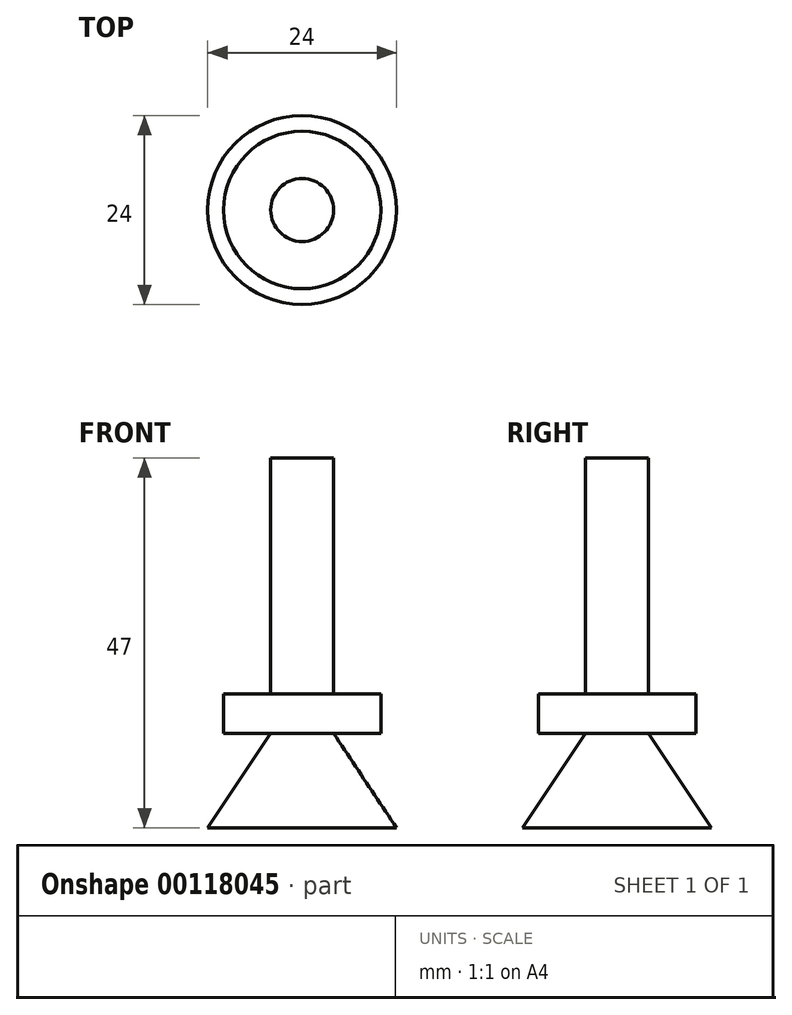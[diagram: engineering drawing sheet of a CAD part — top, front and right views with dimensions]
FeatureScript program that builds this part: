
annotation { "Feature Type Name" : "Feature", "Feature Type Description" : "" }
export const myFeature = defineFeature(function(context is Context, id is Id, definition is map)
    precondition{}
    {
        {
            var Q0;
            Q0=qCreatedBy(makeId("Front.planeOp"),FACE);
            var sketch = newSketch(context, id + "F0", { "sketchPlane" : qUnion([Q0])});
            skLineSegment(sketch, "E0.bottom", {"start": v(0, 0) * mm, "end": v(4, 0) * mm});
            skLineSegment(sketch, "E0.left", {"start": v(0, 0) * mm, "end": v(0, -30) * mm});
            skLineSegment(sketch, "E0.right", {"start": v(4, 0) * mm, "end": v(4, -30) * mm});
            skLineSegment(sketch, "E1", {"start": v(0, -30) * mm, "end": v(0, -47) * mm});
            skLineSegment(sketch, "E2", {"start": v(0, -47) * mm, "end": v(12, -47) * mm});
            skLineSegment(sketch, "E3.bottom", {"start": v(4, -30) * mm, "end": v(10, -30) * mm});
            skLineSegment(sketch, "E3.top", {"start": v(4, -35) * mm, "end": v(10, -35) * mm});
            skLineSegment(sketch, "E3.right", {"start": v(10, -30) * mm, "end": v(10, -35) * mm});
            skLineSegment(sketch, "E4", {"start": v(4, -35) * mm, "end": v(12, -47) * mm});
            skSolve(sketch);
        }
        {
            var Q0;
            Q0=makeQuery(id+"F0.imprint","IMPRINT",FACE,{"disambiguationData":[TD([[makeQuery(id+"F0.imprint","IMPRINT",EDGE,{"derivedFrom":sQuery(id+"F0.wireOp",EDGE,"E0.bottom")}),-1.0]])]});
            var Q1;
            Q1=sQuery(id+"F0.wireOp",EDGE,"E0.left");
            revolve(context, id + "F1", {"entities" : qUnion([Q0]), "axis" : qUnion([Q1]), "revolveType" : RevolveType.FULL});
        }
    });
